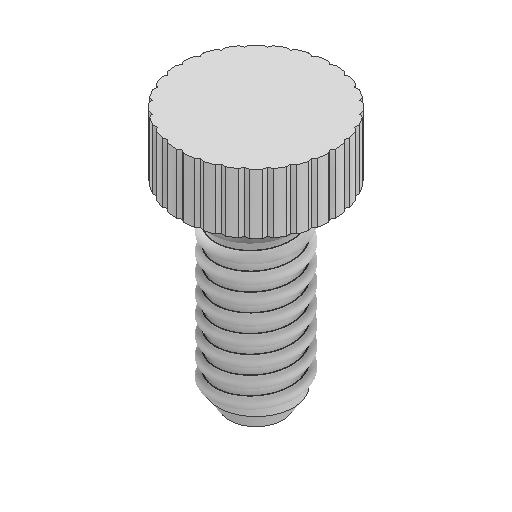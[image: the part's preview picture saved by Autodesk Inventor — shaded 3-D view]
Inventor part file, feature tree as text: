
AUTODESK INVENTOR PART (.ipt)
format: ipt  version: 2025 (Build 290162000, 162)  size: 552,960 bytes
history: native  units: mm
features: sketch x5, extrude x2, helix x1, revolve x1, fillet x1, chamfer x1, projected_geometry x1
ambient origin geometry x8: Origin, YZ Plane, XZ Plane, XY Plane, X Axis, Y Axis, Z Axis, Center Point
bodies: Solid1 (feature_tree)
feature tree (12):
  extrude  "Extrusion1"  Depth=33.0mm TaperAngle=0.0deg
  helix  "Coil1"  [1 undecoded]
  revolve  "Revolution1"  Angle=90.0deg
  fillet  "Fillet1"  Radius=0.5mm
  extrude  "Extrusion2"  Depth=10.0mm TaperAngle=360.0deg
  chamfer  "Chamfer1"  Distance=10.0mm
  sketch  "Sketch1"  dims[d0=12.5mm d1=33.0mm d2=0.0mm d3=1.8mm]
  sketch  "Sketch2"  dims[d5=3.0mm d6=10.0mm d7=100.0mm d8=0.0mm d9=90.0deg d10=90.0deg d11=0.0mm d12=0.0mm d13=90.0deg d14=0.5mm]
  projected_geometry  "Projected Loop1"
  sketch  "Sketch3"  dims[d15=25.4mm d16=280.0mm d18=360.0deg d20=10.0mm d21=0.0mm]
  sketch  "Sketch4"  dims[d22=2.0mm d23=2.0mm d24=45.0deg d17=0.5mm]
  sketch  "Sketch Circular Pattern1"  dims[d4=6.35mm]
note: 1 required parameter value undecoded (feature->parameter linkage not recoverable at this tier; creation-order binding heuristic only, values carry confidence <= 0.55)
